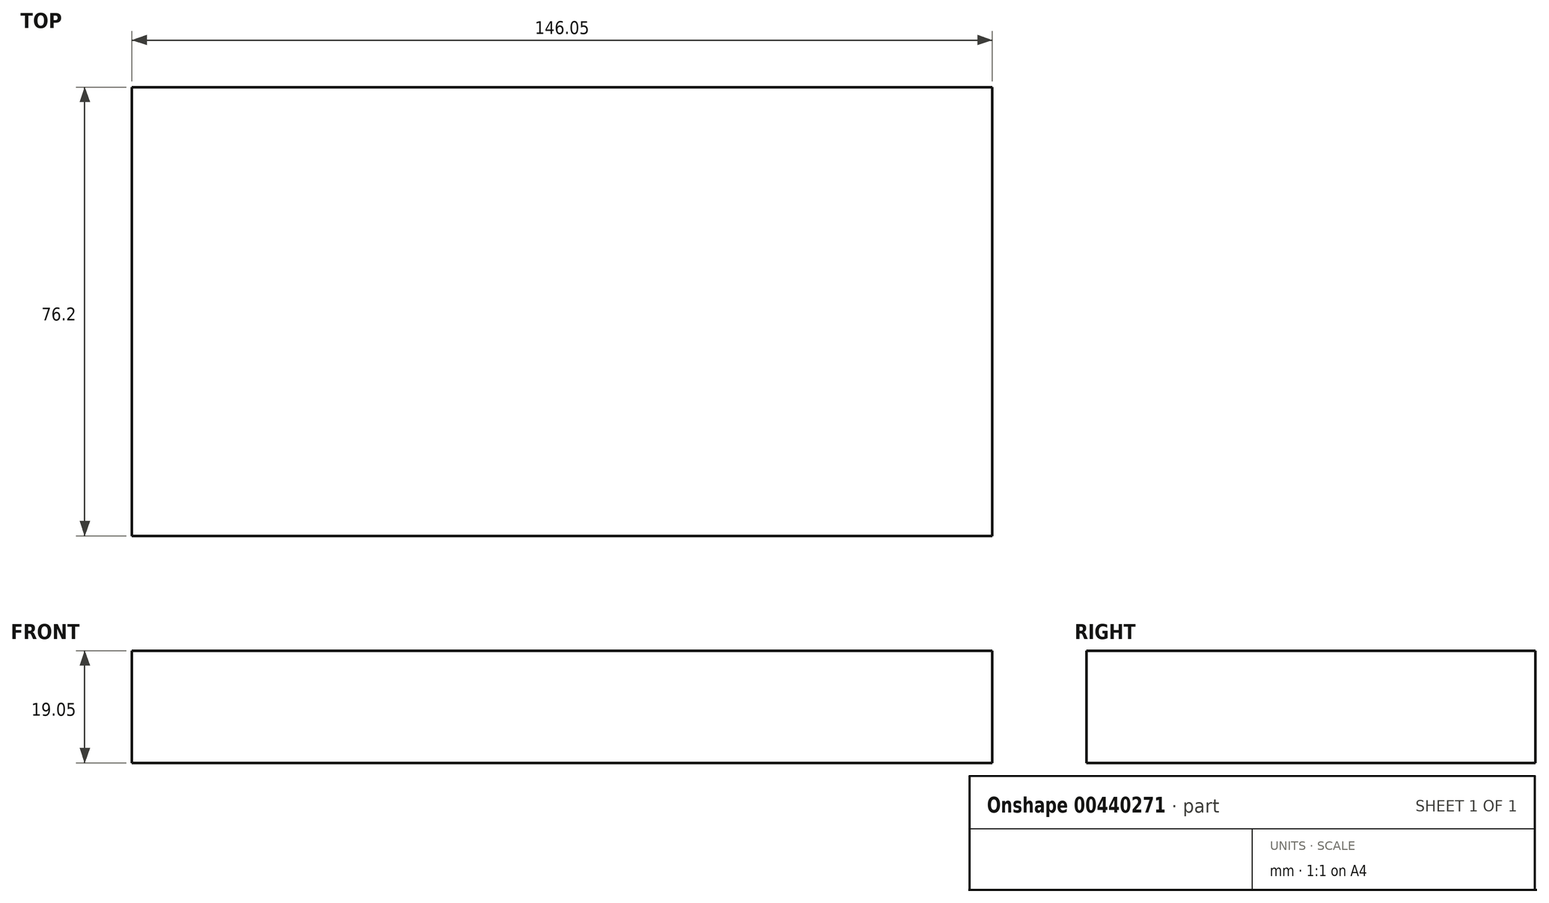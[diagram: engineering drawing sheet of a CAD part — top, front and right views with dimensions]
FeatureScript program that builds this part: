
annotation { "Feature Type Name" : "Feature", "Feature Type Description" : "" }
export const myFeature = defineFeature(function(context is Context, id is Id, definition is map)
    precondition{}
    {
        {
            var Q0;
            Q0=qCreatedBy(makeId("Front.planeOp"),FACE);
            var sketch = newSketch(context, id + "F0", { "sketchPlane" : qUnion([Q0])});
            skLineSegment(sketch, "E0.bottom", {"start": v(-70.84, -12.22) * mm, "end": v(75.2, -12.22) * mm});
            skLineSegment(sketch, "E0.top", {"start": v(-70.84, 6.83) * mm, "end": v(75.2, 6.83) * mm});
            skLineSegment(sketch, "E0.left", {"start": v(-70.84, -12.22) * mm, "end": v(-70.84, 6.83) * mm});
            skLineSegment(sketch, "E0.right", {"start": v(75.2, -12.22) * mm, "end": v(75.2, 6.83) * mm});
            skSolve(sketch);
        }
        {
            var Q0;
            Q0=makeQuery(id+"F0.imprint","IMPRINT",FACE,{"disambiguationData":[TD([[makeQuery(id+"F0.imprint","IMPRINT",EDGE,{"derivedFrom":sQuery(id+"F0.wireOp",EDGE,"E0.bottom")}),1.0]])]});
            extrude(context, id + "F1", {"entities" : qUnion([Q0]), "depth" : 76.2 * mm});
        }
    });
